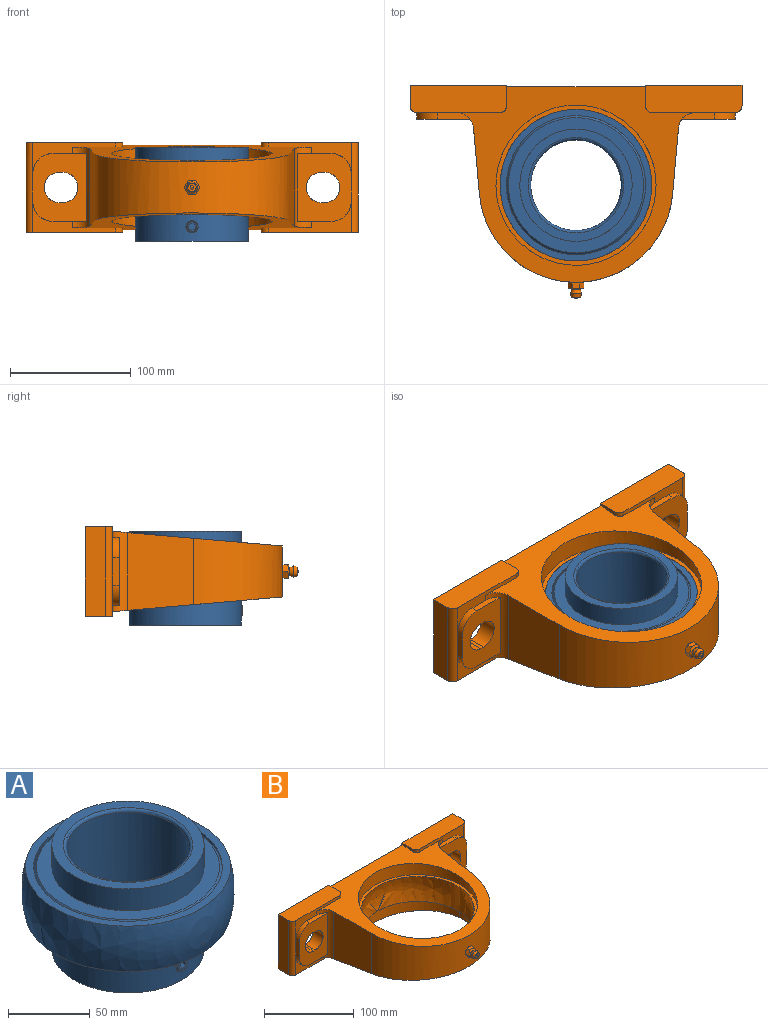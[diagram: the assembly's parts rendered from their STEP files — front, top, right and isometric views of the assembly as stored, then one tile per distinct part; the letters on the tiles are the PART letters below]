
ASSEMBLY  parts=2 mates=1
PART A: 143 faces, bbox 127.1x129.4x131.6 mm
  f0: plane 7.1x6.16mm, normal (0.87,0.5,0), area 38.5mm2, adj f1
  f1: cone r=1.71mm half-angle=45deg, axis (0.87,0.5,0), area 56.6mm2, adj f0,f2
  f2: cylinder r=5mm len=10.05mm, axis (0.87,0.5,0), area 79.3mm2, adj f1,f3
  f3: cylinder r=37.5mm len=75mm, axis (0,0,1), area 17220.6mm2, adj f2,f4,f139,f142
  f4: torus R=39.5mm, axis (0,0,-1), area 754.6mm2, adj f3,f5
  f5: plane 93.01x93.01mm, normal (0,0,-1), area 1887mm2, adj f4,f6
  f6: cylinder r=46.5mm len=93mm, axis (0,0,-1), area 7783.3mm2, adj f5,f7,f105,f106,f107,f108,f109,f110
  f7: sphere r=8.34mm, area 847.9mm2, adj f6,f8,f9,f10,f53,f54,f55,f56
  f8: torus R=51.49mm, axis (0,0,1), area 160.7mm2, adj f7,f9,f95,f106
  f9: torus R=51.49mm, axis (0,0,1), area 160.7mm2, adj f7,f8,f10,f106
  f10: cylinder r=56.49mm len=112.98mm, axis (0,0,1), area 2460.6mm2, adj f7,f9,f11,f13,f15,f17,f19,f21
  f11: torus R=51.49mm, axis (0,0,1), area 160.8mm2, adj f10,f12,f118,f120
  f12: torus R=51.49mm, axis (0,0,1), area 160.7mm2, adj f11,f95,f118,f120
  f13: torus R=51.49mm, axis (0,0,1), area 160.7mm2, adj f10,f14,f116,f118
  f14: torus R=51.49mm, axis (0,0,1), area 160.7mm2, adj f13,f95,f116,f118
  f15: torus R=51.49mm, axis (0,0,1), area 160.7mm2, adj f10,f16,f114,f116
  f16: torus R=51.49mm, axis (0,0,1), area 160.7mm2, adj f15,f95,f114,f116
  f17: torus R=51.49mm, axis (0,0,1), area 160.7mm2, adj f10,f18,f112,f114
  f18: torus R=51.49mm, axis (0,0,1), area 160.7mm2, adj f17,f95,f112,f114
  f19: torus R=51.49mm, axis (0,0,1), area 160.7mm2, adj f10,f20,f110,f112
  f20: torus R=51.49mm, axis (0,0,1), area 160.7mm2, adj f19,f95,f110,f112
  f21: torus R=51.49mm, axis (0,0,1), area 81.7mm2, adj f10,f22,f24,f110
  f22: torus R=51.49mm, axis (0,0,1), area 81.7mm2, adj f21,f23,f95,f110
  f23: torus R=51.49mm, axis (0,0,1), area 78.9mm2, adj f22,f24,f95,f108
  f24: torus R=51.49mm, axis (0,0,1), area 79mm2, adj f10,f21,f23,f108
  f25: torus R=51.49mm, axis (0,0,1), area 160.7mm2, adj f10,f26,f106,f108
  f26: torus R=51.49mm, axis (0,0,1), area 160.7mm2, adj f25,f95,f106,f108
  f27: torus R=51.49mm, axis (0,0,1), area 160.7mm2, adj f10,f28,f135,f137
  f28: torus R=51.49mm, axis (0,0,1), area 160.7mm2, adj f27,f95,f135,f137
  f29: torus R=51.49mm, axis (0,0,1), area 160.7mm2, adj f10,f30,f133,f135
  f30: torus R=51.49mm, axis (0,0,1), area 160.7mm2, adj f29,f95,f133,f135
  f31: torus R=51.49mm, axis (0,0,1), area 160.7mm2, adj f10,f32,f131,f133
  f32: torus R=51.49mm, axis (0,0,1), area 160.7mm2, adj f31,f95,f131,f133
  f33: torus R=51.49mm, axis (0,0,1), area 160.7mm2, adj f10,f34,f129,f131
  f34: torus R=51.49mm, axis (0,0,1), area 160.7mm2, adj f33,f95,f129,f131
  f35: torus R=51.49mm, axis (0,0,1), area 160.7mm2, adj f10,f36,f127,f129
  f36: torus R=51.49mm, axis (0,0,1), area 160.7mm2, adj f35,f95,f127,f129
  f37: torus R=51.49mm, axis (0,0,1), area 160.7mm2, adj f10,f38,f124,f127
  f38: torus R=51.49mm, axis (0,0,1), area 160.7mm2, adj f37,f95,f124,f127
  f39: torus R=51.49mm, axis (0,0,1), area 160.8mm2, adj f10,f40,f122,f124
  f40: torus R=51.49mm, axis (0,0,1), area 160.7mm2, adj f39,f95,f122,f124
  f41: torus R=51.49mm, axis (0,0,1), area 160.8mm2, adj f10,f42,f120,f122
  f42: torus R=51.49mm, axis (0,0,1), area 160.7mm2, adj f41,f95,f120,f122
  f43: cylinder r=0.87mm len=9.02mm, axis (0,-0.97,0.26), area 45.2mm2, adj f10,f44
  f44: sphere r=65mm, area 19597mm2, adj f43,f45
  f45: plane 125.48x125.48mm, normal (0,0,1), area 1907.7mm2, adj f44,f46
  f46: cylinder r=57.62mm len=115.24mm, axis (0,0,1), area 611.8mm2, adj f45,f47
  f47: cone r=55.93mm half-angle=45deg, axis (0,0,1), area 852.6mm2, adj f46,f48
  f48: plane 113.5x113.5mm, normal (0,0,1), area 3025.4mm2, adj f47,f49
  f49: cylinder r=46.51mm len=93.02mm, axis (0,0,-1), area 990.7mm2, adj f48,f50
  f50: plane 115.25x115.25mm, normal (0,0,-1), area 3627.1mm2, adj f49,f51
  f51: cylinder r=57.62mm len=115.24mm, axis (0,0,1), area 3.6mm2, adj f50,f52
  f52: plane 115.25x115.25mm, normal (0,0,1), area 412mm2, adj f10,f51
  f53: torus R=51.49mm, axis (0,0,1), area 160.7mm2, adj f7,f10,f54,f137
  f54: torus R=51.49mm, axis (0,0,1), area 160.7mm2, adj f7,f53,f95,f137
  f55: torus R=51.49mm, axis (0,0,1), area 120.6mm2, adj f7,f56,f137,f138
  f56: cylinder r=46.5mm len=93mm, axis (0,0,-1), area 10888.8mm2, adj f7,f55,f57,f67,f68,f69,f70,f71
  f57: cylinder r=5mm len=10mm, axis (-0.87,-0.5,0), area 4.9mm2, adj f56,f58
  f58: cone r=2.14mm half-angle=45deg, axis (-0.87,-0.5,0), area 37.1mm2, adj f57,f59
  f59: plane 8.28x7.19mm, normal (-0.87,-0.5,0), area 30.7mm2, adj f58,f60,f62,f63,f64,f65,f66
  f60: plane 5.58x4.67mm, normal (-0.25,0.43,0.87), area 14.4mm2, adj f59,f61,f62,f66
  f61: plane 5.77x4.33mm, normal (-0.87,-0.5,0), area 21.7mm2, adj f60,f62,f63,f64,f65,f66
  f62: plane 5.58x4.67mm, normal (0.25,-0.43,0.87), area 14.4mm2, adj f59,f60,f61,f63
  f63: plane 4.33x2.89mm, normal (0.5,-0.87,0), area 14.4mm2, adj f59,f61,f62,f64
  f64: plane 5.58x4.67mm, normal (0.25,-0.43,-0.87), area 14.4mm2, adj f59,f61,f63,f65
  f65: plane 5.58x4.67mm, normal (-0.25,0.43,-0.87), area 14.4mm2, adj f59,f61,f64,f66
  f66: plane 4.33x2.89mm, normal (-0.5,0.87,0), area 14.4mm2, adj f59,f60,f61,f65
  f67: torus R=51.49mm, axis (0,0,1), area 120.6mm2, adj f56,f118,f119,f120
  f68: torus R=51.49mm, axis (0,0,1), area 120.6mm2, adj f56,f116,f117,f118
  f69: torus R=51.49mm, axis (0,0,1), area 120.6mm2, adj f56,f114,f115,f116
  f70: torus R=51.49mm, axis (0,0,1), area 120.6mm2, adj f56,f112,f113,f114
  f71: torus R=51.49mm, axis (0,0,1), area 120.6mm2, adj f56,f110,f111,f112
  f72: torus R=51.49mm, axis (0,0,1), area 120.6mm2, adj f56,f108,f109,f110
  f73: torus R=51.49mm, axis (0,0,1), area 120.6mm2, adj f56,f106,f107,f108
  f74: torus R=51.49mm, axis (0,0,1), area 120.6mm2, adj f56,f135,f136,f137
  f75: torus R=51.49mm, axis (0,0,1), area 120.6mm2, adj f56,f133,f134,f135
  f76: torus R=51.49mm, axis (0,0,1), area 120.6mm2, adj f56,f131,f132,f133
  f77: torus R=51.49mm, axis (0,0,1), area 120.6mm2, adj f56,f129,f130,f131
  f78: torus R=51.49mm, axis (0,0,1), area 120.6mm2, adj f56,f127,f128,f129
  f79: torus R=51.49mm, axis (0,0,1), area 59.1mm2, adj f56,f80,f126,f127
  f80: torus R=51.49mm, axis (0,0,1), area 61.5mm2, adj f56,f79,f124,f125
  f81: torus R=51.49mm, axis (0,0,1), area 120.6mm2, adj f56,f122,f123,f124
  f82: torus R=51.49mm, axis (0,0,1), area 120.6mm2, adj f56,f120,f121,f122
  f83: plane 93.01x93.01mm, normal (0,0,1), area 1887mm2, adj f56,f142
  f84: cylinder r=5mm len=10mm, axis (0,1,0), area 4.9mm2, adj f56,f85
  f85: cone r=4.08mm half-angle=45deg, axis (0,1,0), area 37.1mm2, adj f84,f86
  f86: plane 8.28x8.28mm, normal (0,1,0), area 30.7mm2, adj f85,f87,f89,f90,f91,f92,f93
  f87: plane 5x2.5mm, normal (0.5,0,0.87), area 14.4mm2, adj f86,f88,f89,f93
  f88: plane 5.77x5mm, normal (0,1,0), area 21.7mm2, adj f87,f89,f90,f91,f92,f93
  f89: plane 5x2.5mm, normal (-0.5,0,0.87), area 14.4mm2, adj f86,f87,f88,f90
  f90: plane 5x2.89mm, normal (-1,0,0), area 14.4mm2, adj f86,f88,f89,f91
  f91: plane 5x2.5mm, normal (-0.5,0,-0.87), area 14.4mm2, adj f86,f88,f90,f92
  f92: plane 5x2.5mm, normal (0.5,0,-0.87), area 14.4mm2, adj f86,f88,f91,f93
  f93: plane 5x2.89mm, normal (1,0,0), area 14.4mm2, adj f86,f87,f88,f92
  f94: torus R=51.49mm, axis (0,0,1), area 120.6mm2, adj f7,f56,f105,f106
  f95: cylinder r=56.49mm len=112.98mm, axis (0,0,1), area 2463.2mm2, adj f7,f8,f12,f14,f16,f18,f20,f22
  f96: plane 115.25x115.25mm, normal (0,0,-1), area 397.7mm2, adj f95,f97
  f97: cylinder r=57.62mm len=115.24mm, axis (0,0,1), area 3.6mm2, adj f96,f98
  f98: plane 116.6x116.6mm, normal (0,0,1), area 3638.6mm2, adj f97,f99
  f99: cylinder r=46.51mm len=93.02mm, axis (0,0,1), area 990.7mm2, adj f98,f100
  f100: plane 113.5x113.5mm, normal (0,0,-1), area 3025.4mm2, adj f99,f101
  f101: cone r=55.93mm half-angle=45deg, axis (0,0,-1), area 852.6mm2, adj f100,f102
  f102: cylinder r=57.62mm len=115.24mm, axis (0,0,1), area 611.8mm2, adj f101,f103
  f103: plane 125.48x125.48mm, normal (0,0,-1), area 1909mm2, adj f102,f104
  f104: sphere r=65mm, area 19599.5mm2, adj f103
  f105: torus R=51.49mm, axis (0,0,1), area 120.6mm2, adj f6,f7,f94,f106
  f106: sphere r=8.34mm, area 847.9mm2, adj f6,f8,f9,f10,f25,f26,f56,f73
  f107: torus R=51.49mm, axis (0,0,1), area 120.6mm2, adj f6,f73,f106,f108
  f108: sphere r=8.34mm, area 847.9mm2, adj f6,f10,f23,f24,f25,f26,f56,f72
  f109: torus R=51.49mm, axis (0,0,1), area 120.6mm2, adj f6,f72,f108,f110
  f110: sphere r=8.34mm, area 847.9mm2, adj f6,f10,f19,f20,f21,f22,f56,f71
  f111: torus R=51.49mm, axis (0,0,1), area 120.6mm2, adj f6,f71,f110,f112
  f112: sphere r=8.34mm, area 847.9mm2, adj f6,f10,f17,f18,f19,f20,f56,f70
  f113: torus R=51.49mm, axis (0,0,1), area 120.6mm2, adj f6,f70,f112,f114
  f114: sphere r=8.34mm, area 847.9mm2, adj f6,f10,f15,f16,f17,f18,f56,f69
  f115: torus R=51.49mm, axis (0,0,1), area 120.6mm2, adj f6,f69,f114,f116
  f116: sphere r=8.34mm, area 847.9mm2, adj f6,f10,f13,f14,f15,f16,f56,f68
  f117: torus R=51.49mm, axis (0,0,1), area 120.6mm2, adj f6,f68,f116,f118
  f118: sphere r=8.34mm, area 847.9mm2, adj f6,f10,f11,f12,f13,f14,f56,f67
  f119: torus R=51.49mm, axis (0,0,1), area 120.6mm2, adj f6,f67,f118,f120
  f120: sphere r=8.34mm, area 847.9mm2, adj f6,f10,f11,f12,f41,f42,f56,f67
  f121: torus R=51.49mm, axis (0,0,1), area 120.6mm2, adj f6,f82,f120,f122
  f122: sphere r=8.34mm, area 847.9mm2, adj f6,f10,f39,f40,f41,f42,f56,f81
  f123: torus R=51.49mm, axis (0,0,1), area 120.6mm2, adj f6,f81,f122,f124
  f124: sphere r=8.34mm, area 847.9mm2, adj f6,f10,f37,f38,f39,f40,f56,f80
  f125: torus R=51.49mm, axis (0,0,1), area 61.5mm2, adj f6,f80,f124,f126
  f126: torus R=51.49mm, axis (0,0,1), area 59.1mm2, adj f6,f79,f125,f127
  f127: sphere r=8.34mm, area 847.9mm2, adj f6,f10,f35,f36,f37,f38,f56,f78
  f128: torus R=51.49mm, axis (0,0,1), area 120.6mm2, adj f6,f78,f127,f129
  f129: sphere r=8.34mm, area 847.9mm2, adj f6,f10,f33,f34,f35,f36,f56,f77
  f130: torus R=51.49mm, axis (0,0,1), area 120.6mm2, adj f6,f77,f129,f131
  f131: sphere r=8.34mm, area 847.9mm2, adj f6,f10,f31,f32,f33,f34,f56,f76
  f132: torus R=51.49mm, axis (0,0,1), area 120.6mm2, adj f6,f76,f131,f133
  f133: sphere r=8.34mm, area 847.9mm2, adj f6,f10,f29,f30,f31,f32,f56,f75
  f134: torus R=51.49mm, axis (0,0,1), area 120.6mm2, adj f6,f75,f133,f135
  f135: sphere r=8.34mm, area 847.9mm2, adj f6,f10,f27,f28,f29,f30,f56,f74
  f136: torus R=51.49mm, axis (0,0,1), area 120.6mm2, adj f6,f74,f135,f137
  f137: sphere r=8.34mm, area 847.9mm2, adj f6,f10,f27,f28,f53,f54,f55,f56
  f138: torus R=51.49mm, axis (0,0,1), area 120.6mm2, adj f6,f7,f55,f137
  f139: cylinder r=5mm len=10mm, axis (0,-1,0), area 79.3mm2, adj f3,f140
  f140: cone r=3.5mm half-angle=45deg, axis (0,-1,0), area 56.6mm2, adj f139,f141
  f141: plane 7.1x7.1mm, normal (0,-1,0), area 38.5mm2, adj f140
  f142: torus R=39.5mm, axis (0,0,-1), area 754.6mm2, adj f3,f83
PART B: 83 faces, bbox 315.1x216.6x170.1 mm
  f0: plane 65.39x49.89mm, normal (0,1,0), area 2651.8mm2, adj f8,f9,f10,f11,f13,f14,f15,f16
  f1: plane 65.39x49.89mm, normal (0,1,0), area 2651.8mm2, adj f3,f4,f5,f6,f18,f19,f20,f21
  f2: sphere r=65.01mm, area 12961.5mm2, adj f24,f27
  f3: plane 49.5x12.6mm, normal (1,0,0), area 623.7mm2, adj f1,f4,f6,f31
  f4: plane 65x12.6mm, normal (0,0,1), area 819mm2, adj f1,f3,f5,f31
  f5: plane 49.5x12.6mm, normal (-1,0,0), area 623.7mm2, adj f1,f4,f6,f31
  f6: plane 65x12.6mm, normal (0,0,-1), area 819mm2, adj f1,f3,f5,f31
  f7: plane 74x16.8mm, normal (1,0,0), area 1243.2mm2, adj f29,f30,f31,f32
  f8: plane 49.5x12.6mm, normal (1,0,0), area 623.7mm2, adj f0,f9,f11,f33
  f9: plane 65x12.6mm, normal (0,0,1), area 819mm2, adj f0,f8,f10,f33
  f10: plane 49.5x12.6mm, normal (-1,0,0), area 623.7mm2, adj f0,f9,f11,f33
  f11: plane 65x12.6mm, normal (0,0,-1), area 819mm2, adj f0,f8,f10,f33
  f12: plane 74x16.8mm, normal (-1,0,0), area 1243.2mm2, adj f33,f34,f35,f36
  f13: plane 15.4x3mm, normal (0,0,1), area 46.2mm2, adj f0,f14,f16,f39
  f14: cylinder r=12.5mm len=25mm, axis (0,-1,0), area 604.8mm2, adj f0,f13,f15,f39
  f15: plane 15.4x3mm, normal (0,0,-1), area 46.2mm2, adj f0,f14,f16,f39
  f16: cylinder r=12.5mm len=25mm, axis (0,-1,0), area 604.8mm2, adj f0,f13,f15,f39
  f17: plane 22.52x5.6mm, normal (-1,0,0), area 126.1mm2, adj f26,f36,f37,f39
  f18: plane 15.4x3mm, normal (0,0,1), area 46.2mm2, adj f1,f19,f21,f42
  f19: cylinder r=12.5mm len=25mm, axis (0,-1,0), area 604.8mm2, adj f1,f18,f20,f42
  f20: plane 15.4x3mm, normal (0,0,-1), area 46.2mm2, adj f1,f19,f21,f42
  f21: cylinder r=12.5mm len=25mm, axis (0,-1,0), area 604.8mm2, adj f1,f18,f20,f42
  f22: plane 22.52x5.6mm, normal (1,0,0), area 126.1mm2, adj f25,f28,f29,f42
  f23: sphere r=2.11mm, area 8.9mm2, adj f44
  f24: plane 172.74x172.74mm, normal (0,0,-1), area 1506mm2, adj f2,f45,f46
  f25: cylinder r=16.89mm len=16.89mm, axis (0,1,0), area 148.6mm2, adj f22,f41,f42,f47
  f26: cylinder r=16.89mm len=16.89mm, axis (0,1,0), area 148.6mm2, adj f17,f39,f40,f48
  f27: plane 172.74x172.74mm, normal (0,0,1), area 1506mm2, adj f2,f51
  f28: cylinder r=16.89mm len=16.89mm, axis (0,1,0), area 148.6mm2, adj f22,f42,f43,f52
  f29: cylinder r=5.6mm len=74mm, axis (0,0,1), area 650.9mm2, adj f7,f22,f30,f32,f47,f52
  f30: plane 80.35x22.75mm, normal (0,0,1), area 1778.7mm2, adj f7,f29,f31,f52,f53,f54
  f31: plane 80x74mm, normal (0,1,0), area 2702.5mm2, adj f3,f4,f5,f6,f7,f30,f32,f54
  f32: plane 80.35x22.75mm, normal (0,0,-1), area 1778.5mm2, adj f7,f29,f31,f47,f50,f54
  f33: plane 80x74mm, normal (0,1,0), area 2702.5mm2, adj f8,f9,f10,f11,f12,f34,f35,f56
  f34: plane 80.35x22.75mm, normal (0,0,-1), area 1778.7mm2, adj f12,f33,f36,f48,f49,f56
  f35: plane 80.35x22.75mm, normal (0,0,1), area 1778.5mm2, adj f12,f33,f36,f56,f57,f58
  f36: cylinder r=5.6mm len=74mm, axis (0,0,1), area 650.9mm2, adj f12,f17,f34,f35,f48,f58
  f37: cylinder r=16.89mm len=16.89mm, axis (0,1,0), area 148.6mm2, adj f17,f38,f39,f58
  f38: plane 27.73x5.93mm, normal (0,0,1), area 134.6mm2, adj f37,f39,f58,f59
  f39: plane 56.3x44.3mm, normal (0,-1,0), area 1805.6mm2, adj f13,f14,f15,f16,f17,f26,f37,f38
  f40: plane 27.74x5.93mm, normal (0,0,-1), area 134.6mm2, adj f26,f39,f48,f59
  f41: plane 27.65x5.84mm, normal (0,0,-1), area 134.6mm2, adj f25,f42,f47,f61
  f42: plane 56.3x44.3mm, normal (0,-1,0), area 1805.6mm2, adj f18,f19,f20,f21,f22,f25,f28,f41
  f43: plane 27.65x5.84mm, normal (0,0,1), area 134.6mm2, adj f28,f42,f52,f61
  f44: plane 7.06x7.06mm, normal (0,-1,0), area 30.6mm2, adj f23,f62
  f45: cylinder r=66.31mm len=132.62mm, axis (0,0,1), area 3063mm2, adj f24,f46,f63
  f46: cylinder r=66.31mm len=132.62mm, axis (0,0,1), area 1706.5mm2, adj f24,f45,f63
  f47: plane 68.8x25.74mm, normal (0,-1,0), area 487.9mm2, adj f25,f29,f32,f41,f50,f61,f63
  f48: plane 68.8x25.74mm, normal (0,-1,0), area 487.9mm2, adj f26,f34,f36,f40,f49,f59,f63
  f49: cylinder r=5.6mm len=5.6mm, axis (0,0,1), area 30.8mm2, adj f34,f48,f56,f63
  f50: cylinder r=5.6mm len=5.6mm, axis (0,0,-1), area 30.8mm2, adj f32,f47,f54,f63
  f51: cylinder r=66.31mm len=132.62mm, axis (0,0,-1), area 4442.1mm2, adj f27,f65
  f52: plane 68.8x25.74mm, normal (0,-1,0), area 487.9mm2, adj f28,f29,f30,f43,f53,f61,f65
  f53: cylinder r=5.6mm len=5.6mm, axis (0,0,-1), area 30.8mm2, adj f30,f52,f54,f65
  f54: plane 74x16.8mm, normal (-1,0,0), area 164mm2, adj f30,f31,f32,f50,f53,f55,f63,f65
  f55: plane 115x70.18mm, normal (0,1,0), area 8070.8mm2, adj f54,f56,f63,f65
  f56: plane 74x16.8mm, normal (1,0,0), area 164mm2, adj f33,f34,f35,f49,f55,f57,f63,f65
  f57: cylinder r=5.6mm len=5.6mm, axis (0,0,1), area 30.8mm2, adj f35,f56,f58,f65
  f58: plane 68.8x25.74mm, normal (0,-1,0), area 487.9mm2, adj f35,f36,f37,f38,f57,f59,f65
  f59: cylinder r=14mm len=66.51mm, axis (0,0,-1), area 627.5mm2, adj f38,f39,f40,f48,f58,f60,f63,f65
  f60: plane 64.3x54.43mm, normal (-1,-0.09,0), area 3256.2mm2, adj f59,f63,f65,f67
  f61: cylinder r=14mm len=66.51mm, axis (0,0,-1), area 627.5mm2, adj f41,f42,f43,f47,f52,f63,f64,f65
  f62: cone r=4.62mm half-angle=20deg, axis (0,1,0), area 84.4mm2, adj f44,f66
  f63: plane 205.48x169.85mm, normal (0,-0.09,-1), area 8924.4mm2, adj f45,f46,f47,f48,f49,f50,f54,f55
  f64: plane 64.3x54.43mm, normal (1,-0.09,0), area 3256.2mm2, adj f61,f63,f65,f67
  f65: plane 205.48x169.85mm, normal (0,-0.09,1), area 8912mm2, adj f51,f52,f53,f54,f55,f56,f57,f58
  f66: cone r=4.62mm half-angle=15deg, axis (0,-1,0), area 95.9mm2, adj f62,f71
  f67: cylinder r=80.4mm len=160.19mm, axis (0,0,1), area 12121.7mm2, adj f60,f63,f64,f65,f74
  f68: plane 7.55x7.01mm, normal (0.87,0,-0.5), area 30.1mm2, adj f69,f71,f72,f77,f78
  f69: plane 8.41x7.01mm, normal (0,0,-1), area 30.1mm2, adj f68,f70,f71,f78,f79
  f70: plane 7.55x7.01mm, normal (-0.87,0,-0.5), area 30.1mm2, adj f69,f71,f73,f75,f79
  f71: cone r=3.66mm half-angle=60deg, axis (0,1,0), area 101mm2, adj f66,f68,f69,f70,f72,f73,f80
  f72: plane 7.55x7.01mm, normal (0.87,0,0.5), area 30.1mm2, adj f68,f71,f76,f77,f80
  f73: plane 7.55x7.01mm, normal (-0.87,0,0.5), area 30.1mm2, adj f70,f71,f75,f80,f82
  f74: cylinder r=3.98mm len=7.96mm, axis (0,1,0), area 1.5mm2, adj f67,f81
  f75: cone r=5.56mm half-angle=60deg, axis (0,-1,0), area 3mm2, adj f70,f73,f81
  f76: cone r=5.56mm half-angle=60deg, axis (0,-1,0), area 3mm2, adj f72,f80,f81
  f77: cone r=5.56mm half-angle=60deg, axis (0,-1,0), area 3mm2, adj f68,f72,f81
  f78: cone r=5.56mm half-angle=60deg, axis (0,-1,0), area 2.6mm2, adj f68,f69,f81
  f79: cone r=5.56mm half-angle=60deg, axis (0,-1,0), area 3mm2, adj f69,f70,f81
  f80: plane 8.41x7.01mm, normal (0,0,1), area 30.1mm2, adj f71,f72,f73,f76,f82
  f81: plane 11.3x11.3mm, normal (0,1,0), area 47.5mm2, adj f74,f75,f76,f77,f78,f79,f82
  f82: cone r=5.56mm half-angle=60deg, axis (0,-1,0), area 2.6mm2, adj f73,f80,f81
PLACE A at identity
PLACE B at identity
MATE fastened A.f121 <-> B.f45  axis (0,0,-1) through (108.5,-82.6,-44.5)mm
